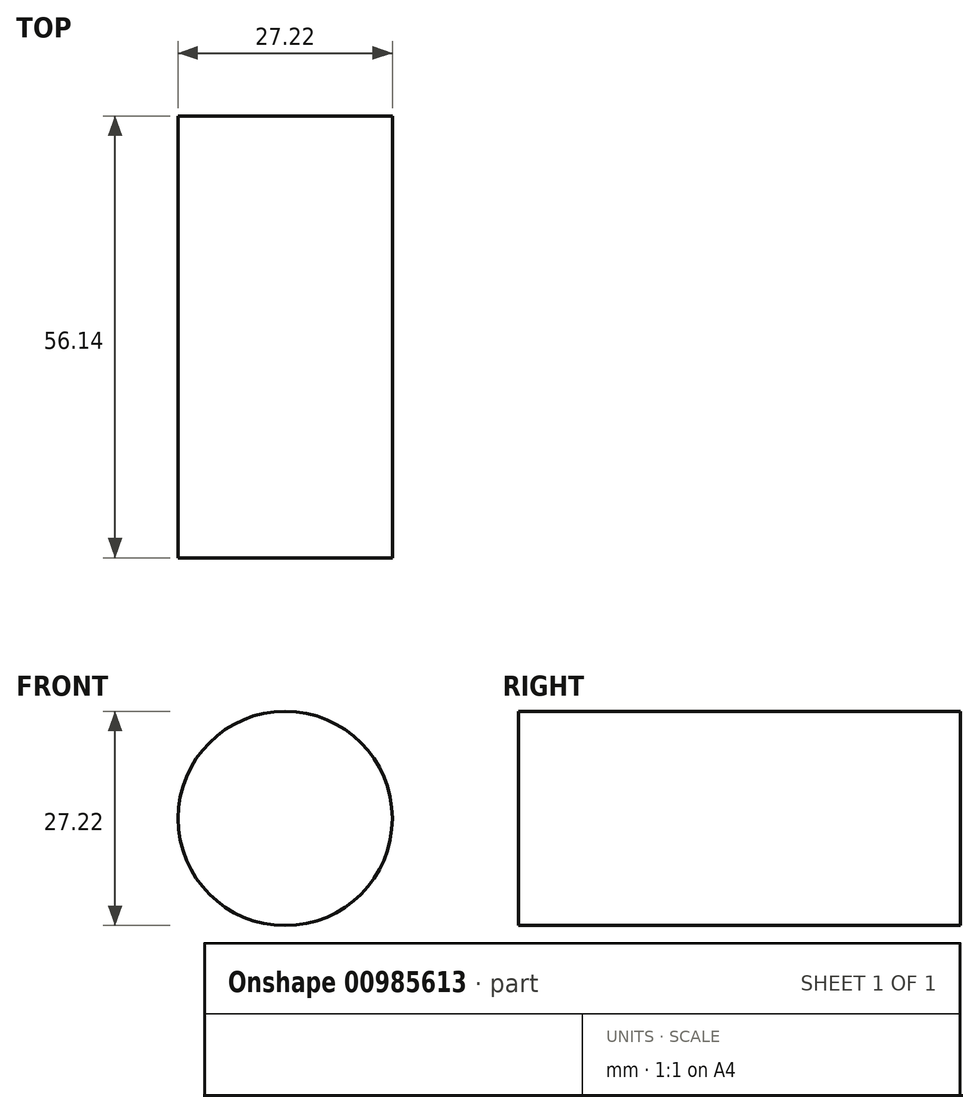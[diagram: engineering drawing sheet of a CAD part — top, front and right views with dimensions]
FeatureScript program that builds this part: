
annotation { "Feature Type Name" : "Feature", "Feature Type Description" : "" }
export const myFeature = defineFeature(function(context is Context, id is Id, definition is map)
    precondition{}
    {
        {
            var Q0;
            Q0=qCreatedBy(makeId("Front.planeOp"),FACE);
            var sketch = newSketch(context, id + "F0", { "sketchPlane" : qUnion([Q0])});
            skCircle(sketch, "E0", {"center": v(0, 0) * mm, "radius": 32.16 * mm});
            skSolve(sketch);
        }
        {
            var Q0;
            Q0=qCreatedBy(makeId("Front.planeOp"),FACE);
            var sketch = newSketch(context, id + "F1", { "sketchPlane" : qUnion([Q0])});
            skCircle(sketch, "E1", {"center": v(0, 0) * mm, "radius": 13.6 * mm});
            skSolve(sketch);
        }
        {
            var Q0;
            Q0=makeQuery(id+"F1.imprint","IMPRINT",FACE,{"disambiguationData":[TD([[makeQuery(id+"F1.imprint","IMPRINT",EDGE,{"derivedFrom":sQuery(id+"F1.wireOp",EDGE,"E1")}),1.0]])]});
            extrude(context, id + "F2", {"entities" : qUnion([Q0]), "oppositeDirection" : true, "depth" : 36.07 * mm, "offsetDistance" : 25.4 * mm});
        }
        {
            var Q0;
            Q0=sQuery(id+"F0.wireOp",EDGE,"E0");
            extrude(context, id + "F3", {"bodyType" : ToolBodyType.SURFACE, "surfaceEntities" : qUnion([Q0]), "oppositeDirection" : true, "depth" : 22.1 * mm, "offsetDistance" : 25.4 * mm});
        }
        {
            var Q0;
            Q0=makeQuery(id+"F2.opExtrude","CAP_FACE",FACE,{"disambiguationData":[OSD([sQuery(id+"F1.wireOp",EDGE,"E1")])],"isStart":false});
            extrude(context, id + "F4", {"entities" : qUnion([Q0]), "operationType" : NewBodyOperationType.ADD, "oppositeDirection" : true, "depth" : 36.58 * mm, "offsetDistance" : 25.4 * mm});
        }
        {
            var Q0;
            Q0=makeQuery(id+"F2.opExtrude","CAP_FACE",FACE,{"disambiguationData":[OSD([sQuery(id+"F1.wireOp",EDGE,"E1")])],"isStart":false});
            extrude(context, id + "F5", {"entities" : qUnion([Q0]), "operationType" : NewBodyOperationType.ADD, "oppositeDirection" : true, "depth" : 56.13 * mm, "offsetDistance" : 25.4 * mm});
        }
    });
